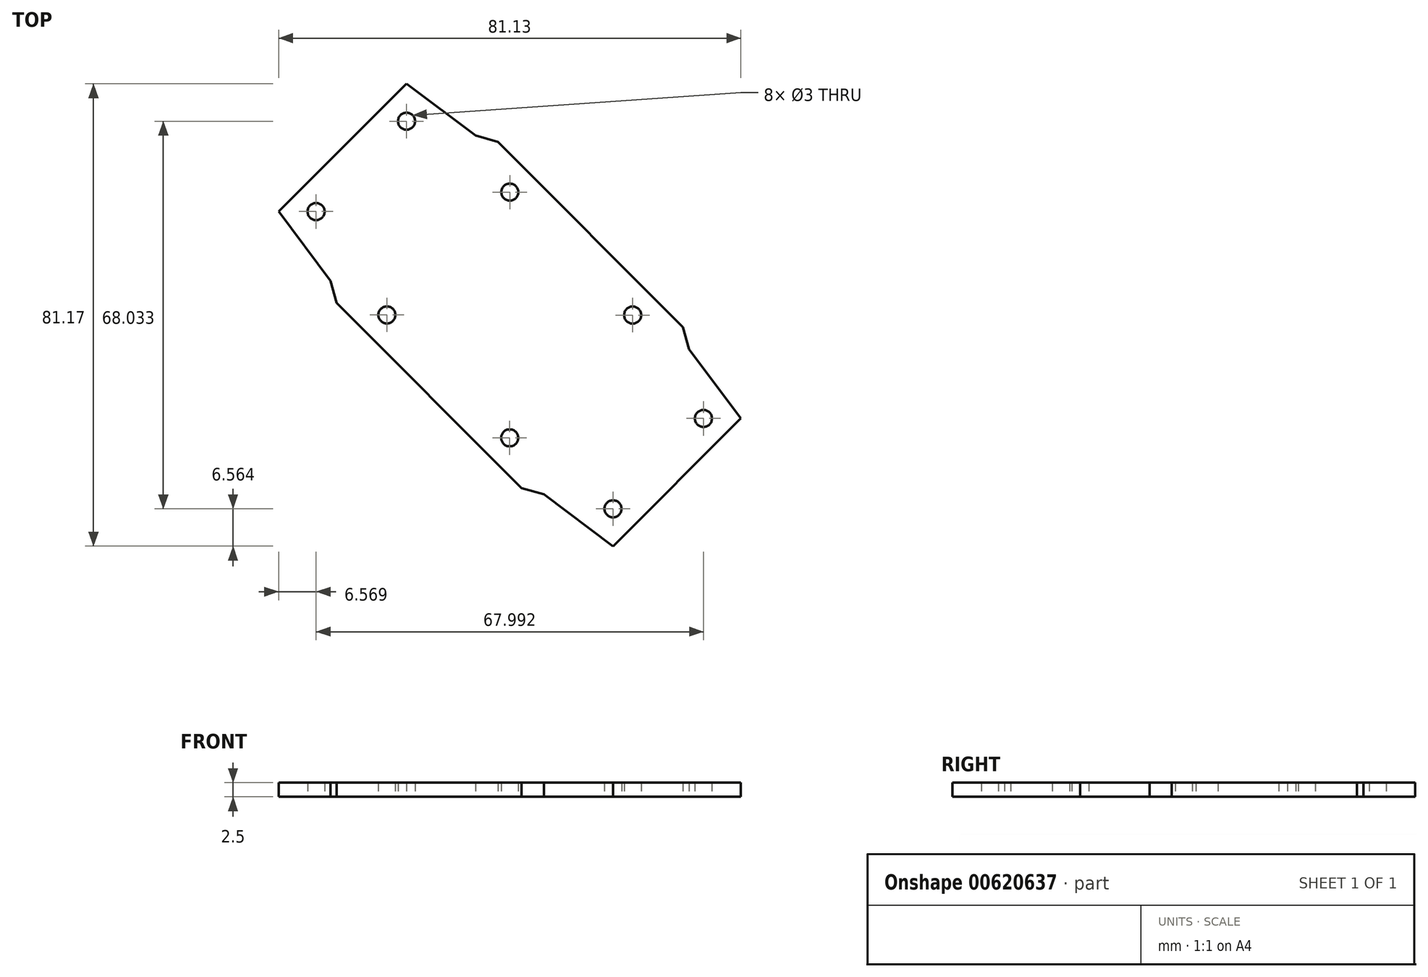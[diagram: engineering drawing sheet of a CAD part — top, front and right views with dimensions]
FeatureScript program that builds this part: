
annotation { "Feature Type Name" : "Feature", "Feature Type Description" : "" }
export const myFeature = defineFeature(function(context is Context, id is Id, definition is map)
    precondition{}
    {
        {
            var Q0;
            Q0=qCreatedBy(makeId("Top.planeOp"),FACE);
            var sketch = newSketch(context, id + "F0", { "sketchPlane" : qUnion([Q0])});
            skPoint(sketch, "E0.middle", {"position": v(5.44, 0.36) * mm});
            skLineSegment(sketch, "E1", {"start": v(7.53, -30.01) * mm, "end": v(11.43, -31.13) * mm});
            skLineSegment(sketch, "E2", {"start": v(11.43, -31.13) * mm, "end": v(23.57, -40.22) * mm});
            skPoint(sketch, "E3.endSnap0", {"position": v(34.79, -29.02) * mm});
            skLineSegment(sketch, "E4", {"start": v(34.79, -29.02) * mm, "end": v(5.44, 0.36) * mm, "construction": true});
            skLineSegment(sketch, "E5", {"start": v(23.57, -40.22) * mm, "end": v(34.79, -29.02) * mm});
            skLineSegment(sketch, "E6", {"start": v(5.44, 0.36) * mm, "end": v(-8.7, -13.77) * mm, "construction": true});
            skLineSegment(sketch, "E7.MirrorCS", {"start": v(35.82, -1.76) * mm, "end": v(36.93, -5.66) * mm});
            skLineSegment(sketch, "E8.MirrorCS", {"start": v(36.93, -5.66) * mm, "end": v(46, -17.8) * mm});
            skLineSegment(sketch, "E9.MirrorCS", {"start": v(46, -17.8) * mm, "end": v(34.79, -29.02) * mm});
            skCircle(sketch, "E10", {"center": v(5.43, -21.2) * mm, "radius": 1.5 * mm});
            skCircle(sketch, "E11.MirrorC", {"center": v(27.01, 0.35) * mm, "radius": 1.5 * mm});
            skCircle(sketch, "E12", {"center": v(23.57, -33.66) * mm, "radius": 1.5 * mm});
            skCircle(sketch, "E13.MirrorC", {"center": v(39.44, -17.8) * mm, "radius": 1.5 * mm});
            skLineSegment(sketch, "E14.MirrorCS", {"start": v(5.44, 0.36) * mm, "end": v(19.6, 14.5) * mm, "construction": true});
            skLineSegment(sketch, "E15", {"start": v(-8.7, -13.77) * mm, "end": v(3.33, -25.83) * mm});
            skLineSegment(sketch, "E16.MirrorCS", {"start": v(19.6, 14.5) * mm, "end": v(31.63, 2.44) * mm});
            skLineSegment(sketch, "E17.MirrorCS", {"start": v(-0.54, 31.85) * mm, "end": v(-12.68, 40.95) * mm});
            skLineSegment(sketch, "E18.MirrorCS", {"start": v(-23.9, 29.74) * mm, "end": v(5.44, 0.36) * mm, "construction": true});
            skLineSegment(sketch, "E19.MirrorCS", {"start": v(-24.93, 2.48) * mm, "end": v(-26.04, 6.38) * mm});
            skLineSegment(sketch, "E20.MirrorCS", {"start": v(19.6, 14.5) * mm, "end": v(7.56, 26.55) * mm});
            skCircle(sketch, "E21.MirrorC", {"center": v(5.46, 21.93) * mm, "radius": 1.5 * mm});
            skCircle(sketch, "E22.MirrorC", {"center": v(-16.12, 0.37) * mm, "radius": 1.5 * mm});
            skPoint(sketch, "E23.MirrorP", {"position": v(-23.9, 29.74) * mm});
            skCircle(sketch, "E24.MirrorC", {"center": v(-28.55, 18.52) * mm, "radius": 1.5 * mm});
            skLineSegment(sketch, "E25.MirrorCS", {"start": v(-35.12, 18.53) * mm, "end": v(-23.9, 29.74) * mm});
            skCircle(sketch, "E26.MirrorC", {"center": v(-12.68, 34.38) * mm, "radius": 1.5 * mm});
            skLineSegment(sketch, "E27.MirrorCS", {"start": v(-26.04, 6.38) * mm, "end": v(-35.12, 18.53) * mm});
            skLineSegment(sketch, "E28.MirrorCS", {"start": v(-8.7, -13.77) * mm, "end": v(-20.75, -1.72) * mm});
            skLineSegment(sketch, "E29.MirrorCS", {"start": v(3.36, 30.74) * mm, "end": v(-0.54, 31.85) * mm});
            skLineSegment(sketch, "E30.MirrorCS", {"start": v(-12.68, 40.95) * mm, "end": v(-23.9, 29.74) * mm});
            skLineSegment(sketch, "E31", {"start": v(-24.93, 2.48) * mm, "end": v(7.53, -30.01) * mm});
            skLineSegment(sketch, "E32", {"start": v(3.36, 30.74) * mm, "end": v(35.82, -1.76) * mm});
            skSolve(sketch);
        }
        {
            var Q0;
            Q0=makeQuery(id+"F0.imprint","IMPRINT",FACE,{"disambiguationData":[TD([[makeQuery(id+"F0.imprint","IMPRINT",EDGE,{"derivedFrom":sQuery(id+"F0.wireOp",EDGE,"E1")}),1.0]])]});
            extrude(context, id + "F1", {"entities" : qUnion([Q0]), "depth" : 2.5 * mm, "offsetDistance" : 25 * mm});
        }
    });
